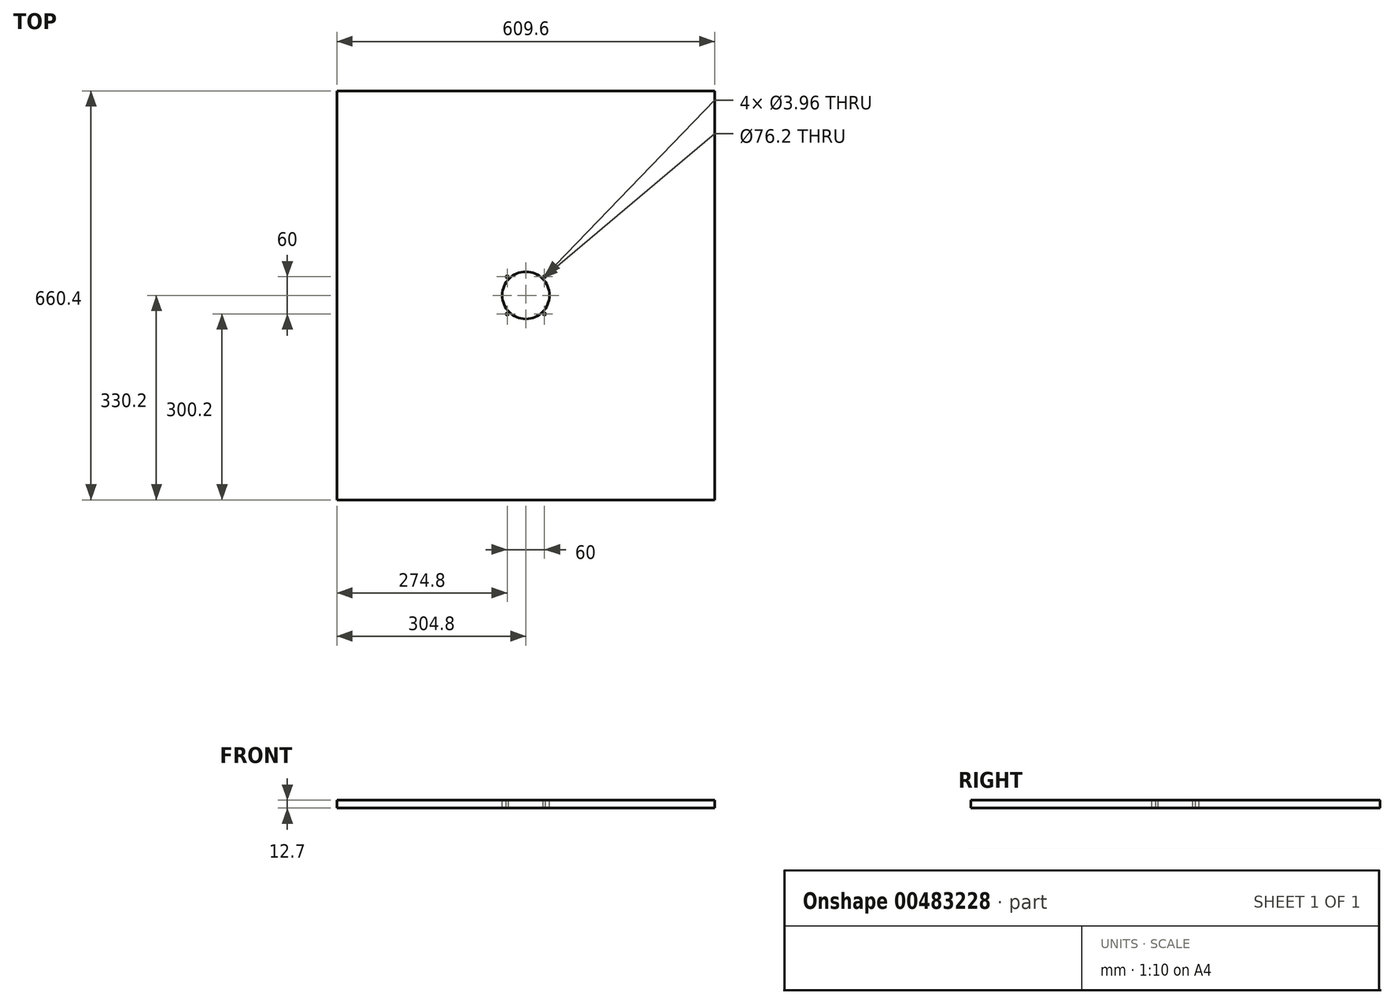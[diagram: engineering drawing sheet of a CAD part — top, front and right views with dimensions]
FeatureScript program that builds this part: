
annotation { "Feature Type Name" : "Feature", "Feature Type Description" : "" }
export const myFeature = defineFeature(function(context is Context, id is Id, definition is map)
    precondition{}
    {
        {
            var Q0;
            Q0=qCreatedBy(makeId("Top.planeOp"),FACE);
            var sketch = newSketch(context, id + "F0", { "sketchPlane" : qUnion([Q0])});
            skLineSegment(sketch, "E0.bottom", {"start": v(304.8, 330.2) * mm, "end": v(-304.8, 330.2) * mm});
            skLineSegment(sketch, "E0.top", {"start": v(304.8, -330.2) * mm, "end": v(-304.8, -330.2) * mm});
            skLineSegment(sketch, "E0.left", {"start": v(304.8, 330.2) * mm, "end": v(304.8, -330.2) * mm});
            skLineSegment(sketch, "E0.right", {"start": v(-304.8, 330.2) * mm, "end": v(-304.8, -330.2) * mm});
            skPoint(sketch, "E0.middle", {"position": v(0, 0) * mm});
            skSolve(sketch);
        }
        {
            var Q0;
            Q0 = qSketchRegion(id + "F0", true);
            extrude(context, id + "F1", {"entities" : qUnion([Q0]), "depth" : 12.7 * mm});
        }
        {
            var Q0;
            Q0=makeQuery(id+"F1.opExtrude","CAP_FACE",FACE,{"disambiguationData":[OSD([sQuery(id+"F0.wireOp",EDGE,"E0.bottom"),sQuery(id+"F0.wireOp",EDGE,"E0.top"),sQuery(id+"F0.wireOp",EDGE,"E0.left"),sQuery(id+"F0.wireOp",EDGE,"E0.right")])],"isStart":false});
            var sketch = newSketch(context, id + "F2", { "sketchPlane" : qUnion([Q0])});
            skCircle(sketch, "E1", {"center": v(0, 0) * mm, "radius": 38.1 * mm});
            skLineSegment(sketch, "E2.bottom", {"start": v(30, 30) * mm, "end": v(-30, 30) * mm, "construction": true});
            skLineSegment(sketch, "E2.top", {"start": v(30, -30) * mm, "end": v(-30, -30) * mm, "construction": true});
            skLineSegment(sketch, "E2.left", {"start": v(30, 30) * mm, "end": v(30, -30) * mm, "construction": true});
            skLineSegment(sketch, "E2.right", {"start": v(-30, 30) * mm, "end": v(-30, -30) * mm, "construction": true});
            skCircle(sketch, "E3", {"center": v(30, 30) * mm, "radius": 1.98 * mm});
            skCircle(sketch, "E4", {"center": v(-30, 30) * mm, "radius": 1.98 * mm});
            skCircle(sketch, "E5", {"center": v(-30, -30) * mm, "radius": 1.98 * mm});
            skCircle(sketch, "E6", {"center": v(30, -30) * mm, "radius": 1.98 * mm});
            skSolve(sketch);
        }
        {
            var Q0;
            Q0 = qSketchRegion(id + "F2", true);
            extrude(context, id + "F3", {"entities" : qUnion([Q0]), "operationType" : NewBodyOperationType.REMOVE, "endBound" : BoundingType.THROUGH_ALL, "oppositeDirection" : true, "depth" : 25.4 * mm});
        }
    });
